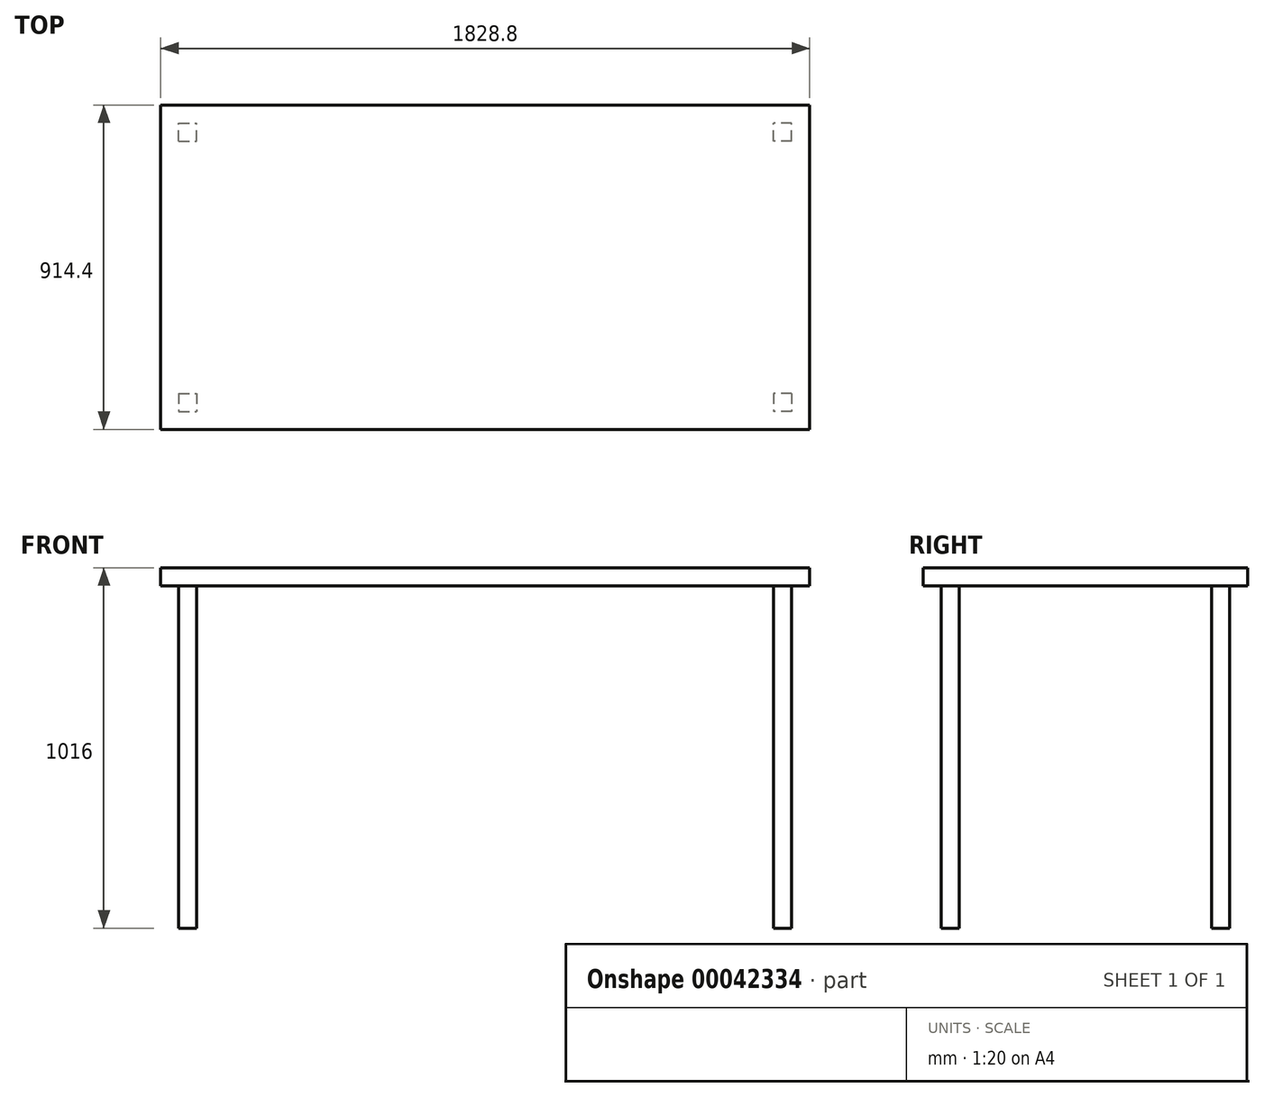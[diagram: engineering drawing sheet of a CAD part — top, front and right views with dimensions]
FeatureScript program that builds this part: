
annotation { "Feature Type Name" : "Feature", "Feature Type Description" : "" }
export const myFeature = defineFeature(function(context is Context, id is Id, definition is map)
    precondition{}
    {
        {
            var Q0;
            Q0=qCreatedBy(makeId("Top.planeOp"),FACE);
            var sketch = newSketch(context, id + "F0", { "sketchPlane" : qUnion([Q0])});
            skLineSegment(sketch, "E0.bottom", {"start": v(-914.4, 457.2) * mm, "end": v(914.4, 457.2) * mm});
            skLineSegment(sketch, "E0.top", {"start": v(-914.4, -457.2) * mm, "end": v(914.4, -457.2) * mm});
            skLineSegment(sketch, "E0.left", {"start": v(-914.4, 457.2) * mm, "end": v(-914.4, -457.2) * mm});
            skLineSegment(sketch, "E0.right", {"start": v(914.4, 457.2) * mm, "end": v(914.4, -457.2) * mm});
            skSolve(sketch);
        }
        {
            var Q0;
            Q0 = qSketchRegion(id + "F0", true);
            extrude(context, id + "F1", {"entities" : qUnion([Q0]), "depth" : 50.8 * mm});
        }
        {
            var Q0;
            Q0=makeQuery(id+"F1.opExtrude","CAP_FACE",FACE,{"disambiguationData":[OSD([sQuery(id+"F0.wireOp",EDGE,"E0.bottom"),sQuery(id+"F0.wireOp",EDGE,"E0.top"),sQuery(id+"F0.wireOp",EDGE,"E0.left"),sQuery(id+"F0.wireOp",EDGE,"E0.right")])],"isStart":false});
            var sketch = newSketch(context, id + "F2", { "sketchPlane" : qUnion([Q0])});
            skLineSegment(sketch, "E1.bottom", {"start": v(-863.6, -355.6) * mm, "end": v(-812.8, -355.6) * mm});
            skLineSegment(sketch, "E1.top", {"start": v(-863.6, -406.4) * mm, "end": v(-812.8, -406.4) * mm});
            skLineSegment(sketch, "E1.left", {"start": v(-863.6, -355.6) * mm, "end": v(-863.6, -406.4) * mm});
            skLineSegment(sketch, "E1.right", {"start": v(-812.8, -355.6) * mm, "end": v(-812.8, -406.4) * mm});
            skSolve(sketch);
        }
        {
            var Q0;
            Q0=makeQuery(id+"F2.imprint","IMPRINT",FACE,{"disambiguationData":[TD([[makeQuery(id+"F2.imprint","IMPRINT",EDGE,{"derivedFrom":sQuery(id+"F2.wireOp",EDGE,"E1.bottom")}),-1.0]])]});
            extrude(context, id + "F3", {"entities" : qUnion([Q0]), "operationType" : NewBodyOperationType.ADD, "oppositeDirection" : true, "depth" : 1016 * mm});
        }
        {
            var Q0;
            Q0=makeQuery(id+"F1.opExtrude","SWEPT_BODY",BODY,{"disambiguationData":[OSD([sQuery(id+"F0.wireOp",EDGE,"E0.bottom"),sQuery(id+"F0.wireOp",EDGE,"E0.top"),sQuery(id+"F0.wireOp",EDGE,"E0.left"),sQuery(id+"F0.wireOp",EDGE,"E0.right")])]});
            var Q1;
            Q1=qCreatedBy(makeId("Front.planeOp"),FACE);
            mirror(context, id + "F4", {"operationType" : NewBodyOperationType.ADD, "entities" : qUnion([Q0]), "mirrorPlane" : qUnion([Q1])});
        }
        {
            var Q0;
            Q0=makeQuery(id+"F1.opExtrude","SWEPT_BODY",BODY,{"disambiguationData":[OSD([sQuery(id+"F0.wireOp",EDGE,"E0.bottom"),sQuery(id+"F0.wireOp",EDGE,"E0.top"),sQuery(id+"F0.wireOp",EDGE,"E0.left"),sQuery(id+"F0.wireOp",EDGE,"E0.right")])]});
            var Q1;
            Q1=qCreatedBy(makeId("Right.planeOp"),FACE);
            mirror(context, id + "F5", {"operationType" : NewBodyOperationType.ADD, "entities" : qUnion([Q0]), "mirrorPlane" : qUnion([Q1])});
        }
    });
